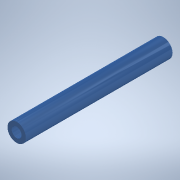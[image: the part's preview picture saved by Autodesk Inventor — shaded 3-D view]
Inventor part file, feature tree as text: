
AUTODESK INVENTOR PART (.ipt)
format: ipt  version: 2020 (Build 240168000, 168)  size: 103,424 bytes
history: native  units: in
note: dims shown in document units (in); Inventor stores cm internally (conversion verified against a paired STEP export)
features: extrude x1, sketch x1
ambient origin geometry x8: Origin, YZ Plane, XZ Plane, XY Plane, X Axis, Y Axis, Z Axis, Center Point
bodies: Solid1 (feature_tree)
feature tree (2):
  extrude  "Extrusion1"  Depth=3.0in
  sketch  "Sketch1"  dims[d0=0.203in d1=0.375in d2=3.0in d3=0.0in]
